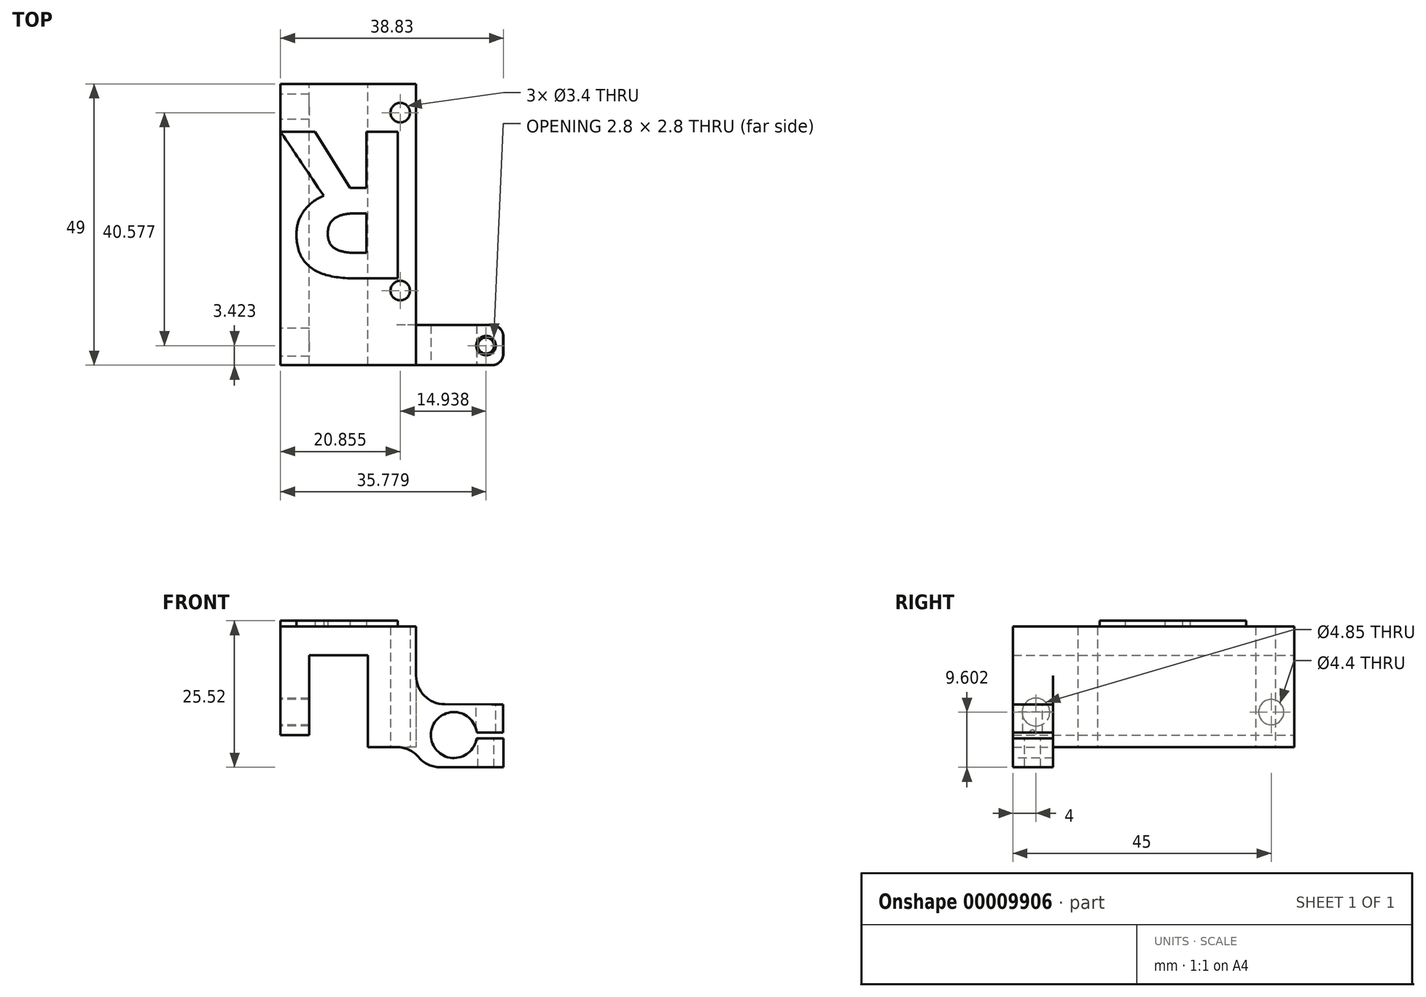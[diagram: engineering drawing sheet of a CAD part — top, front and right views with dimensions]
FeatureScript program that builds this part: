
annotation { "Feature Type Name" : "Feature", "Feature Type Description" : "" }
export const myFeature = defineFeature(function(context is Context, id is Id, definition is map)
    precondition{}
    {
        {
            var Q0;
            Q0=qCreatedBy(makeId("Front.planeOp"),FACE);
            var sketch = newSketch(context, id + "F0", { "sketchPlane" : qUnion([Q0])});
            skLineSegment(sketch, "E0", {"start": v(-18.67, 10.9) * mm, "end": v(-18.67, 29.8) * mm});
            skLineSegment(sketch, "E1", {"start": v(-18.67, 29.8) * mm, "end": v(4.94, 29.8) * mm});
            skLineSegment(sketch, "E2", {"start": v(4.94, 29.8) * mm, "end": v(4.94, 16.27) * mm});
            skLineSegment(sketch, "E3", {"start": v(-3.47, 8.8) * mm, "end": v(-3.47, 24.8) * mm});
            skLineSegment(sketch, "E4", {"start": v(-3.47, 24.8) * mm, "end": v(-13.67, 24.8) * mm});
            skLineSegment(sketch, "E5", {"start": v(-13.67, 24.8) * mm, "end": v(-13.67, 10.9) * mm});
            skLineSegment(sketch, "E6", {"start": v(-13.67, 10.9) * mm, "end": v(-18.67, 10.9) * mm});
            skLineSegment(sketch, "E7", {"start": v(4.94, 16.27) * mm, "end": v(4.94, 8.8) * mm});
            skLineSegment(sketch, "E8", {"start": v(4.94, 8.8) * mm, "end": v(-3.47, 8.8) * mm});
            skLineSegment(sketch, "E9", {"start": v(4.94, 16.27) * mm, "end": v(4.94, 16.27) * mm});
            skLineSegment(sketch, "E10", {"start": v(20.13, 16.24) * mm, "end": v(20.13, 11.34) * mm});
            skLineSegment(sketch, "E11", {"start": v(20.13, 11.34) * mm, "end": v(13.49, 11.34) * mm});
            skLineSegment(sketch, "E12", {"start": v(13.49, 11.34) * mm, "end": v(13.49, 10.34) * mm});
            skLineSegment(sketch, "E13", {"start": v(13.49, 10.34) * mm, "end": v(20.16, 10.34) * mm});
            skLineSegment(sketch, "E14", {"start": v(20.16, 10.34) * mm, "end": v(20.16, 5.29) * mm});
            skLineSegment(sketch, "E15", {"start": v(20.16, 5.29) * mm, "end": v(6.35, 5.29) * mm});
            skLineSegment(sketch, "E16", {"start": v(6.35, 5.29) * mm, "end": v(4.94, 8.8) * mm});
            skLineSegment(sketch, "E17", {"start": v(20.13, 16.24) * mm, "end": v(4.94, 16.27) * mm});
            skSolve(sketch);
        }
        {
            var Q0;
            Q0=makeQuery(id+"F0.imprint","IMPRINT",FACE,{"disambiguationData":[TD([[makeQuery(id+"F0.imprint","IMPRINT",EDGE,{"derivedFrom":sQuery(id+"F0.wireOp",EDGE,"E0")}),-1.0]])]});
            var Q1;
            {var subQ2=sQuery(id+"F0.wireOp",EDGE,"69cbcc5d-e0c3-48db-8baf-3487a8abab7d");Q1=makeQuery(id+"F0.imprint","IMPRINT",FACE,{"disambiguationData":[TD([[makeQuery(id+"F0.imprint","IMPRINT",EDGE,{"derivedFrom":subQ2}),-1.0]])]});}
            var Q2;
            Q2=makeQuery(id+"F0.imprint","IMPRINT",FACE,{"disambiguationData":[TD([[makeQuery(id+"F0.imprint","IMPRINT",EDGE,{"derivedFrom":sQuery(id+"F0.wireOp",EDGE,"E7")}),1.0]])]});
            extrude(context, id + "F1", {"entities" : qUnion([Q0, Q1, Q2]), "depth" : 7 * mm});
        }
        {
            var Q0;
            Q0=makeQuery(id+"F0.imprint","IMPRINT",FACE,{"disambiguationData":[TD([[makeQuery(id+"F0.imprint","IMPRINT",EDGE,{"derivedFrom":sQuery(id+"F0.wireOp",EDGE,"E0")}),-1.0]])]});
            extrude(context, id + "F2", {"entities" : qUnion([Q0]), "operationType" : NewBodyOperationType.ADD, "oppositeDirection" : true, "depth" : 42 * mm});
        }
        {
            var Q0;
            {var subQ0=sQuery(id+"F0.wireOp",EDGE,"E8");Q0=makeQuery(id+"F2.boolean.opBoolean","MERGE",FACE,{"derivedFrom":[makeQuery(id+"F1.opExtrude","SWEPT_FACE",FACE,{"disambiguationData":[OSD([subQ0])]}),makeQuery(id+"F2.opExtrude","SWEPT_FACE",FACE,{"disambiguationData":[OSD([subQ0])]})]});}
            var sketch = newSketch(context, id + "F3", { "sketchPlane" : qUnion([Q0])});
            skCircle(sketch, "E18", {"center": v(2.19, -6) * mm, "radius": 1.7 * mm});
            skCircle(sketch, "E19", {"center": v(2.19, -37) * mm, "radius": 1.7 * mm});
            skCircle(sketch, "E20", {"center": v(17.69, -21.5) * mm, "radius": 11 * mm});
            skSolve(sketch);
        }
        {
            var Q0;
            Q0 = qSketchRegion(id + "F3", true);
            extrude(context, id + "F4", {"entities" : qUnion([Q0]), "operationType" : NewBodyOperationType.REMOVE, "endBound" : BoundingType.THROUGH_ALL, "oppositeDirection" : true, "depth" : 25 * mm});
        }
        {
            var Q0;
            Q0=makeQuery(id+"F1.opExtrude","CAP_FACE",FACE,{"disambiguationData":[OSD([sQuery(id+"F0.wireOp",EDGE,"E0"),sQuery(id+"F0.wireOp",EDGE,"E1"),sQuery(id+"F0.wireOp",EDGE,"E2"),sQuery(id+"F0.wireOp",EDGE,"E3"),sQuery(id+"F0.wireOp",EDGE,"E4"),sQuery(id+"F0.wireOp",EDGE,"E5"),sQuery(id+"F0.wireOp",EDGE,"E6"),sQuery(id+"F0.wireOp",EDGE,"E8"),sQuery(id+"F0.wireOp",EDGE,"E9"),sQuery(id+"F0.wireOp",EDGE,"58f11638-63e7-4b32-8aff-a1ba3c53649b"),sQuery(id+"F0.wireOp",EDGE,"E10"),sQuery(id+"F0.wireOp",EDGE,"E11"),sQuery(id+"F0.wireOp",EDGE,"E12"),sQuery(id+"F0.wireOp",EDGE,"E13"),sQuery(id+"F0.wireOp",EDGE,"E14"),sQuery(id+"F0.wireOp",EDGE,"E15"),sQuery(id+"F0.wireOp",EDGE,"E16")])],"isStart":false});
            var sketch = newSketch(context, id + "F5", { "sketchPlane" : qUnion([Q0])});
            skCircle(sketch, "E21", {"center": v(11.53, 10.9) * mm, "radius": 4 * mm});
            skSolve(sketch);
        }
        {
            var Q0;
            Q0 = qSketchRegion(id + "F5", true);
            extrude(context, id + "F6", {"entities" : qUnion([Q0]), "operationType" : NewBodyOperationType.REMOVE, "oppositeDirection" : true, "depth" : 10 * mm});
        }
        {
            var Q0;
            Q0 = qSketchRegion(id + "F3", true);
            extrude(context, id + "F7", {"entities" : qUnion([Q0]), "operationType" : NewBodyOperationType.REMOVE, "endBound" : BoundingType.THROUGH_ALL, "oppositeDirection" : true, "depth" : 25 * mm});
        }
        {
            var Q0;
            Q0=makeQuery(id+"F1.opExtrude","SWEPT_FACE",FACE,{"disambiguationData":[OSD([sQuery(id+"F0.wireOp",EDGE,"E17")])]});
            var sketch = newSketch(context, id + "F8", { "sketchPlane" : qUnion([Q0])});
            skCircle(sketch, "E22", {"center": v(17.1, -3.58) * mm, "radius": 1.7 * mm});
            skCircle(sketch, "E23", {"center": v(17.1, -3.58) * mm, "radius": 1.4 * mm});
            skSolve(sketch);
        }
        {
            var Q0;
            Q0=makeQuery(id+"F8.imprint","IMPRINT",FACE,{"disambiguationData":[TD([[makeQuery(id+"F8.imprint","IMPRINT",EDGE,{"derivedFrom":sQuery(id+"F8.wireOp",EDGE,"E23")}),1.0]])]});
            extrude(context, id + "F9", {"entities" : qUnion([Q0]), "operationType" : NewBodyOperationType.REMOVE, "endBound" : BoundingType.THROUGH_ALL, "oppositeDirection" : true, "depth" : 25 * mm});
        }
        {
            var Q0;
            Q0=makeQuery(id+"F8.imprint","IMPRINT",FACE,{"disambiguationData":[TD([[makeQuery(id+"F8.imprint","IMPRINT",EDGE,{"derivedFrom":sQuery(id+"F8.wireOp",EDGE,"E22")}),1.0]])]});
            extrude(context, id + "F10", {"entities" : qUnion([Q0]), "operationType" : NewBodyOperationType.REMOVE, "endBound" : BoundingType.UP_TO_NEXT, "oppositeDirection" : true, "depth" : 25 * mm});
        }
        {
            var Q0;
            Q0=makeQuery(id+"F1.opExtrude","SWEPT_EDGE",EDGE,{"disambiguationData":[OSD([sQuery(id+"F0.wireOp",EDGE,"E2"),sQuery(id+"F0.wireOp",EDGE,"E7"),sQuery(id+"F0.wireOp",EDGE,"E17")])]});
            fillet(context, id + "F11", {"entities" : qUnion([Q0]), "radius" : 5 * mm, "tangentPropagation" : true, "allowEdgeOverflow" : false});
        }
        {
            var Q0;
            Q0=makeQuery(id+"F1.opExtrude","SWEPT_EDGE",EDGE,{"disambiguationData":[OSD([sQuery(id+"F0.wireOp",EDGE,"E7"),sQuery(id+"F0.wireOp",EDGE,"E8"),sQuery(id+"F0.wireOp",EDGE,"E16")])]});
            fillet(context, id + "F12", {"entities" : qUnion([Q0]), "radius" : 5 * mm, "tangentPropagation" : true, "allowEdgeOverflow" : false});
        }
        {
            var Q0;
            Q0=makeQuery(id+"F1.opExtrude","SWEPT_EDGE",EDGE,{"disambiguationData":[OSD([sQuery(id+"F0.wireOp",EDGE,"E15"),sQuery(id+"F0.wireOp",EDGE,"E16")])]});
            fillet(context, id + "F13", {"entities" : qUnion([Q0]), "radius" : 5 * mm, "tangentPropagation" : true, "allowEdgeOverflow" : false});
        }
        {
            var Q0;
            Q0=makeQuery(id+"F1.opExtrude","CAP_EDGE",EDGE,{"disambiguationData":[OSD([sQuery(id+"F0.wireOp",EDGE,"E10")])],"isStart":false});
            var Q1;
            Q1=makeQuery(id+"F1.opExtrude","CAP_EDGE",EDGE,{"disambiguationData":[OSD([sQuery(id+"F0.wireOp",EDGE,"E14")])],"isStart":false});
            var Q2;
            Q2=makeQuery(id+"F1.opExtrude","CAP_EDGE",EDGE,{"disambiguationData":[OSD([sQuery(id+"F0.wireOp",EDGE,"E10")])],"isStart":true});
            var Q3;
            Q3=makeQuery(id+"F1.opExtrude","CAP_EDGE",EDGE,{"disambiguationData":[OSD([sQuery(id+"F0.wireOp",EDGE,"E14")])],"isStart":true});
            fillet(context, id + "F14", {"entities" : qUnion([Q0, Q1, Q2, Q3]), "radius" : 2 * mm, "tangentPropagation" : true, "allowEdgeOverflow" : false});
        }
        {
            var Q0;
            {var subQ0=sQuery(id+"F0.wireOp",EDGE,"E0");Q0=makeQuery(id+"F2.boolean.opBoolean","MERGE",FACE,{"derivedFrom":[makeQuery(id+"F1.opExtrude","SWEPT_FACE",FACE,{"disambiguationData":[OSD([subQ0])]}),makeQuery(id+"F2.opExtrude","SWEPT_FACE",FACE,{"disambiguationData":[OSD([subQ0])]})]});}
            var sketch = newSketch(context, id + "F15", { "sketchPlane" : qUnion([Q0])});
            skCircle(sketch, "E24", {"center": v(-38, 14.9) * mm, "radius": 2.2 * mm});
            skCircle(sketch, "E25", {"center": v(3, 14.9) * mm, "radius": 2.43 * mm});
            skSolve(sketch);
        }
        {
            var Q0;
            Q0 = qSketchRegion(id + "F15", true);
            extrude(context, id + "F16", {"entities" : qUnion([Q0]), "operationType" : NewBodyOperationType.REMOVE, "oppositeDirection" : true, "depth" : 6 * mm});
        }
        {
            var Q0;
            {var subQ0=sQuery(id+"F0.wireOp",EDGE,"E1");Q0=makeQuery(id+"F2.boolean.opBoolean","MERGE",FACE,{"derivedFrom":[makeQuery(id+"F1.opExtrude","SWEPT_FACE",FACE,{"disambiguationData":[OSD([subQ0])]}),makeQuery(id+"F2.opExtrude","SWEPT_FACE",FACE,{"disambiguationData":[OSD([subQ0])]})]});}
            var sketch = newSketch(context, id + "F17", { "sketchPlane" : qUnion([Q0])});
            skText(sketch, "E26", { "text": "R", "fontName": "OpenSans-Bold.ttf"});
            const initialGuessF17  = {"E26": [0.00494, 0.03366, -1, 0, 0.02575]};
            skSetInitialGuess(sketch, initialGuessF17);
            skSolve(sketch);
        }
        {
            var Q0;
            Q0 = qSketchRegion(id + "F17", true);
            extrude(context, id + "F18", {"entities" : qUnion([Q0]), "operationType" : NewBodyOperationType.ADD, "depth" : 1 * mm});
        }
    });
